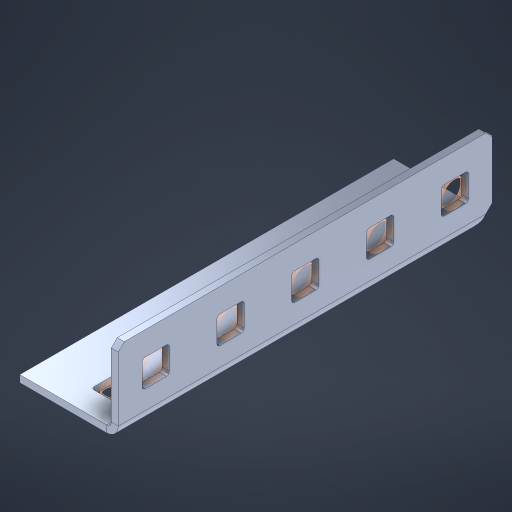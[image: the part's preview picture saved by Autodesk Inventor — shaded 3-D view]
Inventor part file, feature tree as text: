
AUTODESK INVENTOR PART (.ipt)
format: ipt  version: 2023 (Build 270158000, 158)  size: 451,584 bytes
history: native  units: in
note: dims shown in document units (in); Inventor stores cm internally (conversion verified against a paired STEP export)
features: other x15, sheet_metal_op x10, extrude x9, sketch x8, mirror x1, pattern_linear x1, chamfer x1
ambient origin geometry x8: Origin, YZ Plane, XZ Plane, XY Plane, X Axis, Y Axis, Z Axis, Center Point
bodies: Solid1 (feature_tree), Body (feature_tree)
feature tree (45):
  other  "Flange Pattern Plane"
  sheet_metal_op  "Flange Pattern"
  sheet_metal_op  "Body Pattern"
  other  "Arc Length"
  mirror  "Notch Mirror"
  pattern_linear  "Notch Pattern"  Spacing1=0.1875in  [1 undecoded]
  chamfer  "End Chamfer"
  extrude  "Half Cut"  Depth=0.0469in
  sketch  "Sketch1"  dims[d0=2.5in]
  other  "Plate1"
  sketch  "Sketch2"  dims[d1=2.5in]
  other  "Plate2"
  sheet_metal_op  "Bend1"
  sheet_metal_op  "Corner1"
  sketch  "Sketch3"  dims[d2=0.0469in]
  other  "Flange Pattern Sketch"
  sketch  "Sketch7"  dims[d3=0.0469in]
  other  "Srf1"
  other  "Srf2"
  sketch  "Sketch8"  dims[d4=0.0234in]
  sketch  "Sketch9"  dims[d5=0.0938in]
  other  "Srf91"
  sheet_metal_op  "Body Pattern Sketch"
  other  "Srf92"
  sketch  "Sketch13"  dims[d6=0.0469in]
  sketch  "Sketch14"  dims[d7=0.5in d8=90.0deg d9=0.0312in d10=0.1875in d11=0.0469in d12=0.0469in d16=0.182in d17=0.02in d18=0.0469in d19=0.0in d20=0.25in d21=0.25in d46=0.172in d47=1.0in d48=0.0in d49=0.182in d50=0.02in d51=0.25in d52=0.25in d53=0.0469in d54=0.0in d55=0.172in d56=1.0in d57=0.0in d60=1.9685in d62=0.5in d63=0.3937in d65=0.5in d85=0.1227in d86=0.1659in d88=0.04in d89=0.0469in d90=0.0in d91=0.04in d92=0.0491in d95=2.5in d96=0.04in d97=0.25in d98=45.0deg d101=0.0in d102=2.497in d131=0.5in d132=1.9685in d134=0.5in d139=0.5in]
  other  "Srf856"
  other  "Srf1310"
  other  "Srf1311"
  other  "Srf1312"
  other  "Srf1376"
  other  "Srf1377"
  sheet_metal_op  "Flange Stamp"
  sheet_metal_op  "Flange Circle"
  sheet_metal_op  "Body Stamp"
  sheet_metal_op  "Body Circle"
  sheet_metal_op  "Notch"
  extrude  "ExtrusionSrf2"  Depth=0.0469in
  extrude  "ExtrusionSrf92"  Depth=0.5in
  extrude  "ExtrusionSrf856"  Depth=0.02in
  extrude  "ExtrusionSrf1310"  Depth=0.0469in
  extrude  "ExtrusionSrf1311"  TaperAngle=0.0deg  [1 undecoded]
  extrude  "ExtrusionSrf1312"  Depth=0.5in
  extrude  "ExtrusionSrf1376"  Depth=0.5in
  extrude  "ExtrusionSrf1377"  Depth=0.5in
note: 2 required parameter values undecoded (feature->parameter linkage not recoverable at this tier; creation-order binding heuristic only, values carry confidence <= 0.55)
